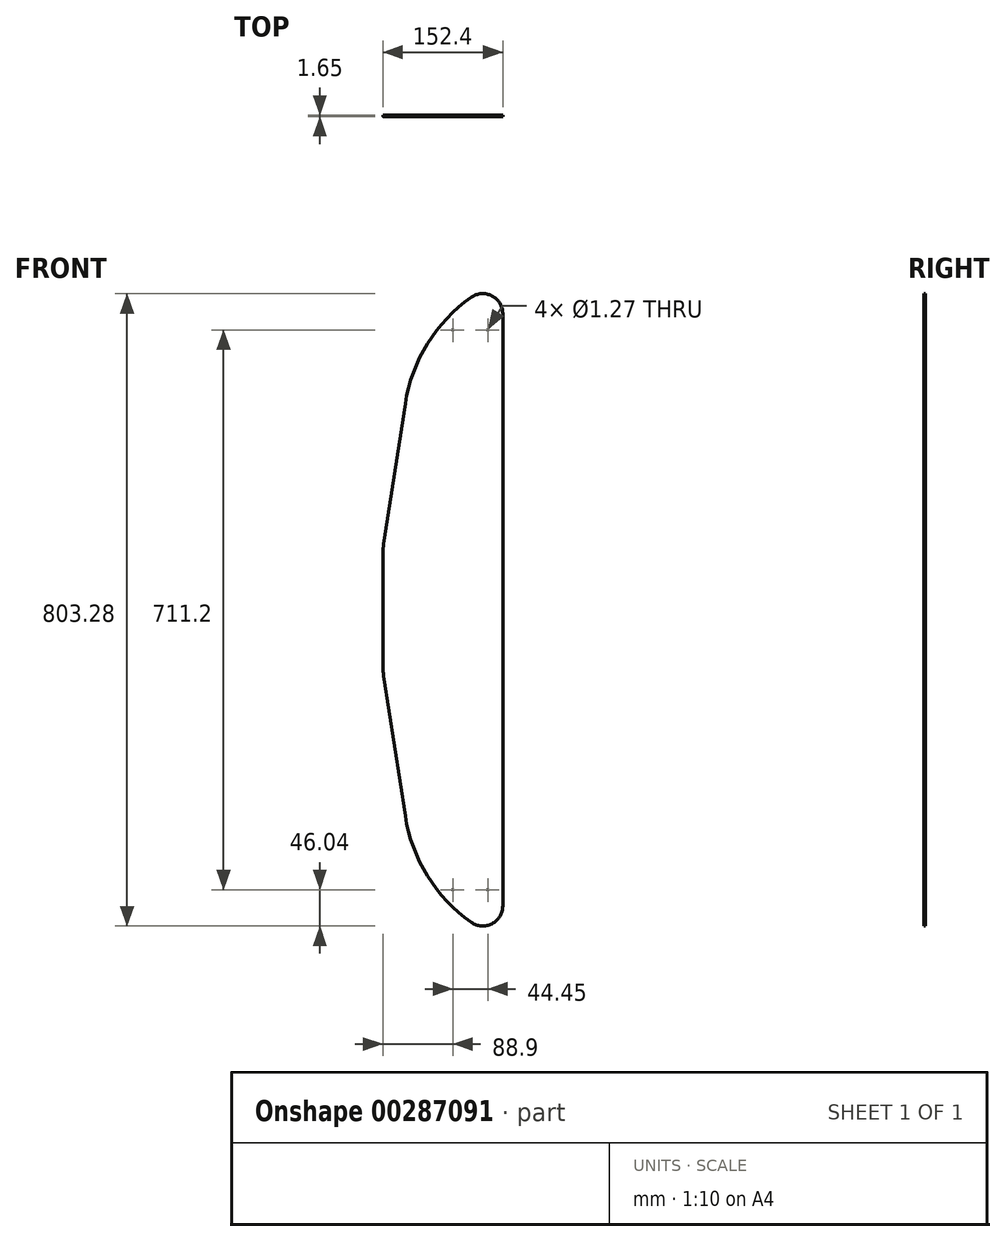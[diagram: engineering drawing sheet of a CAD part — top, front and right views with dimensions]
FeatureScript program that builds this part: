
annotation { "Feature Type Name" : "Feature", "Feature Type Description" : "" }
export const myFeature = defineFeature(function(context is Context, id is Id, definition is map)
    precondition{}
    {
        {
            var Q0;
            Q0=qCreatedBy(makeId("Front.planeOp"),FACE);
            var sketch = newSketch(context, id + "F0", { "sketchPlane" : qUnion([Q0])});
            skLineSegment(sketch, "E0.bottom", {"start": v(50.8, 406.4) * mm, "end": v(76.2, 406.4) * mm});
            skLineSegment(sketch, "E0.top", {"start": v(50.8, -406.4) * mm, "end": v(76.2, -406.4) * mm});
            skLineSegment(sketch, "E0.left", {"start": v(-76.2, 68.43) * mm, "end": v(-76.2, -68.43) * mm});
            skLineSegment(sketch, "E0.right", {"start": v(76.2, 406.4) * mm, "end": v(76.2, -406.4) * mm});
            skLineSegment(sketch, "E1", {"start": v(-75.02, -83.88) * mm, "end": v(-47.65, -261.78) * mm});
            skLineSegment(sketch, "E2", {"start": v(-75.02, 83.88) * mm, "end": v(-47.65, 261.78) * mm});
            skPoint(sketch, "E3.orphan", {"position": v(-76.2, 406.4) * mm});
            skPoint(sketch, "E4.visualSharp", {"position": v(-25.4, 406.4) * mm});
            skPoint(sketch, "E5.visualSharp", {"position": v(-25.4, -406.4) * mm});
            skPoint(sketch, "E6.visualSharp", {"position": v(-76.2, -76.2) * mm});
            skArc(sketch, "E6.filletArc", {"start": v(-76.2, -68.43) * mm, "mid": v(-75.9, -76.18) * mm, "end": v(-75.02, -83.88) * mm});
            skPoint(sketch, "E7.visualSharp", {"position": v(-76.2, 76.2) * mm});
            skArc(sketch, "E7.filletArc", {"start": v(-75.02, 83.88) * mm, "mid": v(-75.9, 76.18) * mm, "end": v(-76.2, 68.43) * mm});
            skArc(sketch, "E8", {"start": v(50.8, 406.4) * mm, "mid": v(-14.79, 345.23) * mm, "end": v(-47.65, 261.78) * mm});
            skArc(sketch, "E9", {"start": v(-47.65, -261.78) * mm, "mid": v(-14.79, -345.23) * mm, "end": v(50.8, -406.4) * mm});
            skSolve(sketch);
        }
        {
            var Q0;
            Q0 = qSketchRegion(id + "F0", true);
            extrude(context, id + "F1", {"entities" : qUnion([Q0]), "depth" : 1.65 * mm});
        }
        {
            var Q0;
            Q0=makeQuery(id+"F1.opExtrude","SWEPT_EDGE",EDGE,{"disambiguationData":[OSD([sQuery(id+"F0.wireOp",EDGE,"E0.bottom"),sQuery(id+"F0.wireOp",EDGE,"E0.right")])]});
            var Q1;
            Q1=makeQuery(id+"F1.opExtrude","SWEPT_EDGE",EDGE,{"disambiguationData":[OSD([sQuery(id+"F0.wireOp",EDGE,"E0.top"),sQuery(id+"F0.wireOp",EDGE,"E0.right")])]});
            fillet(context, id + "F2", {"entities" : qUnion([Q0, Q1]), "radius" : 25.4 * mm, "tangentPropagation" : true, "allowEdgeOverflow" : false});
        }
        {
            var Q0;
            Q0=makeQuery(id+"F2.opFillet","BLEND_EDGE",EDGE,{"blendedFrom":[makeQuery(id+"F1.opExtrude","SWEPT_EDGE",EDGE,{"disambiguationData":[OSD([sQuery(id+"F0.wireOp",EDGE,"E0.bottom"),sQuery(id+"F0.wireOp",EDGE,"E0.right")])]}),makeQuery(id+"F1.opExtrude","SWEPT_FACE",FACE,{"disambiguationData":[OSD([sQuery(id+"F0.wireOp",EDGE,"E8")])]})],"blendedInto":[makeQuery(id+"F1.opExtrude","SWEPT_FACE",FACE,{"disambiguationData":[OSD([sQuery(id+"F0.wireOp",EDGE,"E8")])]})]});
            var Q1;
            Q1=makeQuery(id+"F2.opFillet","BLEND_EDGE",EDGE,{"blendedFrom":[makeQuery(id+"F1.opExtrude","SWEPT_EDGE",EDGE,{"disambiguationData":[OSD([sQuery(id+"F0.wireOp",EDGE,"E0.top"),sQuery(id+"F0.wireOp",EDGE,"E0.right")])]}),makeQuery(id+"F1.opExtrude","SWEPT_FACE",FACE,{"disambiguationData":[OSD([sQuery(id+"F0.wireOp",EDGE,"E9")])]})],"blendedInto":[makeQuery(id+"F1.opExtrude","SWEPT_FACE",FACE,{"disambiguationData":[OSD([sQuery(id+"F0.wireOp",EDGE,"E9")])]})]});
            fillet(context, id + "F3", {"entities" : qUnion([Q0, Q1]), "radius" : 25.4 * mm, "tangentPropagation" : true, "allowEdgeOverflow" : false});
        }
        {
            var Q0;
            Q0=makeQuery(id+"F1.opExtrude","CAP_FACE",FACE,{"disambiguationData":[OSD([sQuery(id+"F0.wireOp",EDGE,"E0.bottom"),sQuery(id+"F0.wireOp",EDGE,"E0.top"),sQuery(id+"F0.wireOp",EDGE,"E0.left"),sQuery(id+"F0.wireOp",EDGE,"E0.right"),sQuery(id+"F0.wireOp",EDGE,"E1"),sQuery(id+"F0.wireOp",EDGE,"E2"),sQuery(id+"F0.wireOp",EDGE,"E6.filletArc"),sQuery(id+"F0.wireOp",EDGE,"E7.filletArc"),sQuery(id+"F0.wireOp",EDGE,"E8"),sQuery(id+"F0.wireOp",EDGE,"E9")])],"isStart":true});
            var sketch = newSketch(context, id + "F4", { "sketchPlane" : qUnion([Q0])});
            skCircle(sketch, "E10", {"center": v(-57.15, 355.6) * mm, "radius": 0.64 * mm});
            skCircle(sketch, "E11", {"center": v(-12.7, 355.6) * mm, "radius": 0.64 * mm});
            skCircle(sketch, "E12.MirrorC", {"center": v(-57.15, -355.6) * mm, "radius": 0.64 * mm});
            skCircle(sketch, "E13.MirrorC", {"center": v(-12.7, -355.6) * mm, "radius": 0.64 * mm});
            skSolve(sketch);
        }
        {
            var Q0;
            Q0 = qSketchRegion(id + "F4", true);
            extrude(context, id + "F5", {"entities" : qUnion([Q0]), "operationType" : NewBodyOperationType.REMOVE, "oppositeDirection" : true, "depth" : 25.4 * mm});
        }
    });
